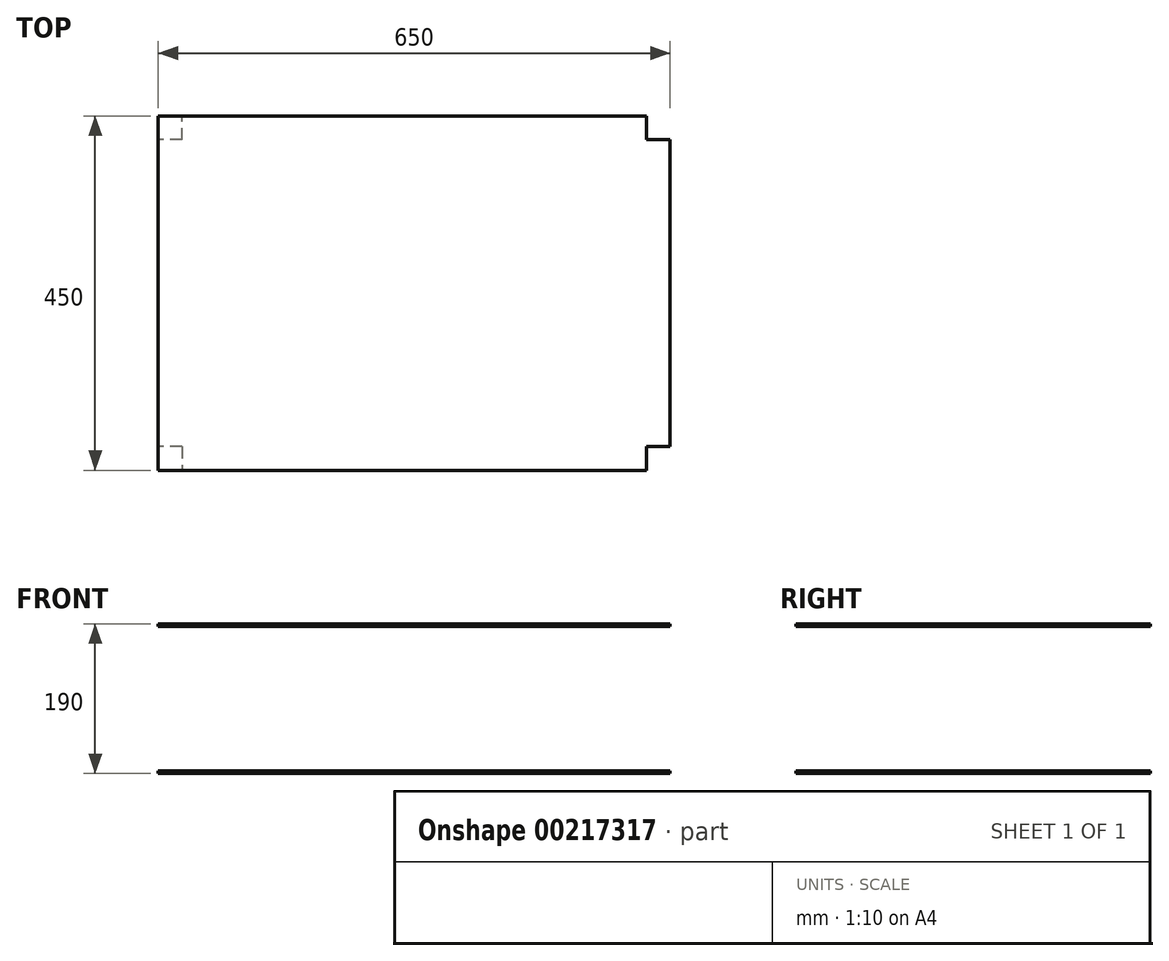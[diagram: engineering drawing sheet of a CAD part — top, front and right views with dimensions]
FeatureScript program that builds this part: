
annotation { "Feature Type Name" : "Feature", "Feature Type Description" : "" }
export const myFeature = defineFeature(function(context is Context, id is Id, definition is map)
    precondition{}
    {
        {
            var Q0;
            Q0=qCreatedBy(makeId("Top.planeOp"),FACE);
            var sketch = newSketch(context, id + "F0", { "sketchPlane" : qUnion([Q0])});
            skLineSegment(sketch, "E0.bottom", {"start": v(325, -225) * mm, "end": v(-325, -225) * mm});
            skLineSegment(sketch, "E0.top", {"start": v(325, 225) * mm, "end": v(-325, 225) * mm});
            skLineSegment(sketch, "E0.left", {"start": v(325, -225) * mm, "end": v(325, 225) * mm});
            skLineSegment(sketch, "E0.right", {"start": v(-325, -225) * mm, "end": v(-325, 225) * mm});
            skPoint(sketch, "E0.middle", {"position": v(0, 0) * mm});
            skLineSegment(sketch, "E1.bottom", {"start": v(295, -195) * mm, "end": v(-295, -195) * mm});
            skLineSegment(sketch, "E1.top", {"start": v(295, 195) * mm, "end": v(-295, 195) * mm});
            skLineSegment(sketch, "E1.left", {"start": v(295, -195) * mm, "end": v(295, 195) * mm});
            skLineSegment(sketch, "E1.right", {"start": v(-295, -195) * mm, "end": v(-295, 195) * mm});
            skLineSegment(sketch, "E2", {"start": v(295, 195) * mm, "end": v(325, 195) * mm});
            skLineSegment(sketch, "E3", {"start": v(325, 195) * mm, "end": v(295, 195) * mm});
            skLineSegment(sketch, "E4", {"start": v(295, 225) * mm, "end": v(295, 195) * mm});
            skLineSegment(sketch, "E5", {"start": v(295, -195) * mm, "end": v(325, -195) * mm});
            skLineSegment(sketch, "E6", {"start": v(325, -195) * mm, "end": v(295, -195) * mm});
            skLineSegment(sketch, "E7", {"start": v(295, -195) * mm, "end": v(295, -225) * mm});
            skLineSegment(sketch, "E8", {"start": v(-295, -195) * mm, "end": v(-295, -225) * mm});
            skLineSegment(sketch, "E9", {"start": v(-295, -195) * mm, "end": v(-325, -195) * mm});
            skLineSegment(sketch, "E10", {"start": v(-295, 195) * mm, "end": v(-325, 195) * mm});
            skLineSegment(sketch, "E11", {"start": v(-295, 195) * mm, "end": v(-295, 225) * mm});
            skSolve(sketch);
        }
        {
            var Q0;
            {var subQ4=sQuery(id+"F0.wireOp",EDGE,"E10");Q0=makeQuery(id+"F0.imprint","IMPRINT",FACE,{"disambiguationData":[TD([[makeQuery(id+"F0.imprint","IMPRINT",EDGE,{"derivedFrom":subQ4}),-1.0]])]});}
            var Q1;
            Q1=makeQuery(id+"F0.imprint","IMPRINT",FACE,{"disambiguationData":[TD([[makeQuery(id+"F0.imprint","IMPRINT",EDGE,{"derivedFrom":sQuery(id+"F0.wireOp",EDGE,"E1.top")}),-1.0]])]});
            var Q2;
            Q2=makeQuery(id+"F0.imprint","IMPRINT",FACE,{"disambiguationData":[TD([[makeQuery(id+"F0.imprint","IMPRINT",EDGE,{"derivedFrom":sQuery(id+"F0.wireOp",EDGE,"E1.bottom")}),-1.0]])]});
            var Q3;
            Q3=makeQuery(id+"F0.imprint","IMPRINT",FACE,{"disambiguationData":[TD([[makeQuery(id+"F0.imprint","IMPRINT",EDGE,{"derivedFrom":sQuery(id+"F0.wireOp",EDGE,"E1.right")}),1.0]])]});
            var Q4;
            {var subQ3=sQuery(id+"F0.wireOp",EDGE,"E8");Q4=makeQuery(id+"F0.imprint","IMPRINT",FACE,{"disambiguationData":[TD([[makeQuery(id+"F0.imprint","IMPRINT",EDGE,{"derivedFrom":subQ3}),-1.0]])]});}
            var Q5;
            Q5=makeQuery(id+"F0.imprint","IMPRINT",FACE,{"disambiguationData":[TD([[makeQuery(id+"F0.imprint","IMPRINT",EDGE,{"derivedFrom":sQuery(id+"F0.wireOp",EDGE,"E1.bottom")}),1.0]])]});
            var Q6;
            Q6=makeQuery(id+"F0.imprint","IMPRINT",FACE,{"disambiguationData":[TD([[makeQuery(id+"F0.imprint","IMPRINT",EDGE,{"derivedFrom":sQuery(id+"F0.wireOp",EDGE,"E1.left")}),-1.0]])]});
            var Q7;
            {var subQ4=sQuery(id+"F0.wireOp",EDGE,"E3");Q7=makeQuery(id+"F0.imprint","IMPRINT",FACE,{"disambiguationData":[TD([[makeQuery(id+"F0.imprint","IMPRINT",EDGE,{"derivedFrom":subQ4}),-1.0]])]});}
            var Q8;
            {var subQ4=sQuery(id+"F0.wireOp",EDGE,"E6");Q8=makeQuery(id+"F0.imprint","IMPRINT",FACE,{"disambiguationData":[TD([[makeQuery(id+"F0.imprint","IMPRINT",EDGE,{"derivedFrom":subQ4}),1.0]])]});}
            extrude(context, id + "F1", {"entities" : qUnion([Q0, Q1, Q2, Q3, Q4, Q5, Q6, Q7, Q8]), "depth" : 3 * mm});
        }
        {
            var Q0;
            Q0=makeQuery(id+"F0.imprint","IMPRINT",FACE,{"disambiguationData":[TD([[makeQuery(id+"F0.imprint","IMPRINT",EDGE,{"derivedFrom":sQuery(id+"F0.wireOp",EDGE,"E1.bottom")}),-1.0]])]});
            var Q1;
            Q1=makeQuery(id+"F0.imprint","IMPRINT",FACE,{"disambiguationData":[TD([[makeQuery(id+"F0.imprint","IMPRINT",EDGE,{"derivedFrom":sQuery(id+"F0.wireOp",EDGE,"E1.right")}),1.0]])]});
            var Q2;
            Q2=makeQuery(id+"F0.imprint","IMPRINT",FACE,{"disambiguationData":[TD([[makeQuery(id+"F0.imprint","IMPRINT",EDGE,{"derivedFrom":sQuery(id+"F0.wireOp",EDGE,"E1.top")}),-1.0]])]});
            var Q3;
            Q3=makeQuery(id+"F0.imprint","IMPRINT",FACE,{"disambiguationData":[TD([[makeQuery(id+"F0.imprint","IMPRINT",EDGE,{"derivedFrom":sQuery(id+"F0.wireOp",EDGE,"E1.bottom")}),1.0]])]});
            var Q4;
            Q4=makeQuery(id+"F0.imprint","IMPRINT",FACE,{"disambiguationData":[TD([[makeQuery(id+"F0.imprint","IMPRINT",EDGE,{"derivedFrom":sQuery(id+"F0.wireOp",EDGE,"E1.left")}),-1.0]])]});
            extrude(context, id + "F2", {"entities" : qUnion([Q0, Q1, Q2, Q3, Q4]), "depth" : 3 * mm});
        }
        {
            var Q0;
            Q0=makeQuery(id+"F1.opExtrude","SWEPT_BODY",BODY,{"disambiguationData":[OSD([sQuery(id+"F0.wireOp",EDGE,"E0.bottom"),sQuery(id+"F0.wireOp",EDGE,"E0.top"),sQuery(id+"F0.wireOp",EDGE,"E0.left"),sQuery(id+"F0.wireOp",EDGE,"E0.right"),sQuery(id+"F0.wireOp",EDGE,"E1.bottom"),sQuery(id+"F0.wireOp",EDGE,"E1.top"),sQuery(id+"F0.wireOp",EDGE,"E1.left"),sQuery(id+"F0.wireOp",EDGE,"E1.right")])]});
            transform(context, id + "F3", {"entities" : qUnion([Q0]), "transformType" : TransformType.TRANSLATION_3D, "dx" : 0 * mm, "dy" : 0 * mm, "dz" : 187 * mm, "makeCopy" : false});
        }
    });
